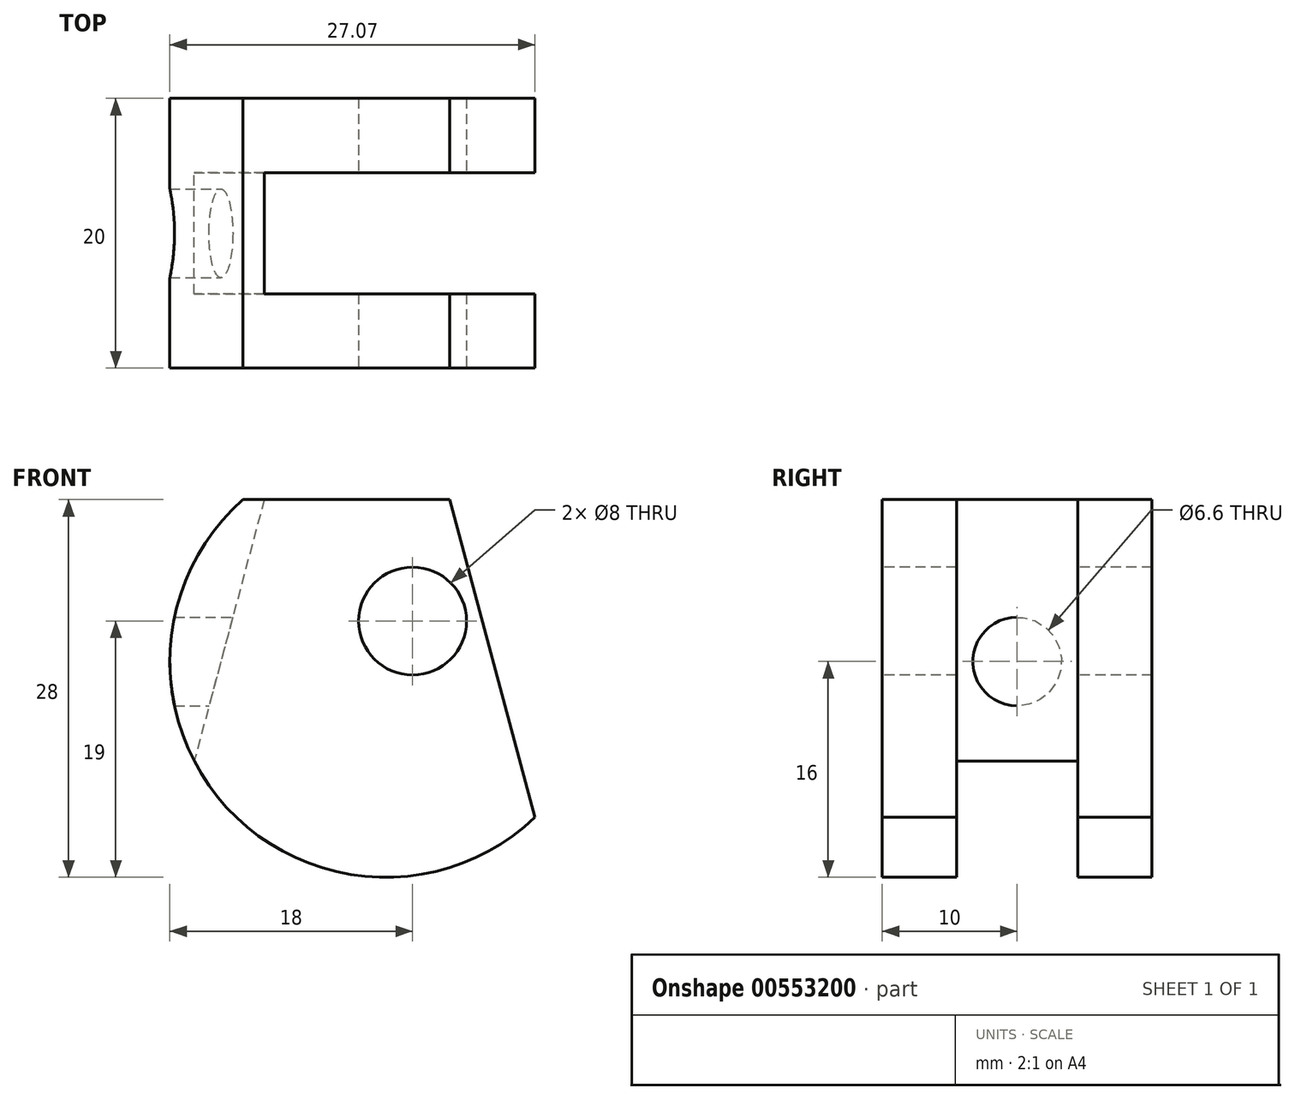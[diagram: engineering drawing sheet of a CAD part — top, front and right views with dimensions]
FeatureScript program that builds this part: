
annotation { "Feature Type Name" : "Feature", "Feature Type Description" : "" }
export const myFeature = defineFeature(function(context is Context, id is Id, definition is map)
    precondition{}
    {
        {
            var Q0;
            Q0=qCreatedBy(makeId("Front.planeOp"),FACE);
            var sketch = newSketch(context, id + "F0", { "sketchPlane" : qUnion([Q0])});
            skArc(sketch, "E0", {"start": v(-10.58, 12) * mm, "mid": v(-11.78, -10.83) * mm, "end": v(11.07, -11.55) * mm});
            skCircle(sketch, "E1", {"center": v(2, 3) * mm, "radius": 4 * mm, "construction": true});
            skLineSegment(sketch, "E2", {"start": v(-10.58, 12) * mm, "end": v(4.76, 12) * mm});
            skLineSegment(sketch, "E3", {"start": v(4.76, 12) * mm, "end": v(11.07, -11.55) * mm});
            skSolve(sketch);
        }
        {
            var Q0;
            Q0=qCreatedBy(makeId("Front.planeOp"),FACE);
            var sketch = newSketch(context, id + "F1", { "sketchPlane" : qUnion([Q0])});
            skLineSegment(sketch, "E4", {"start": v(-9, 12) * mm, "end": v(-16.5, -16) * mm});
            skLineSegment(sketch, "E5", {"start": v(-16.5, -16) * mm, "end": v(11.07, -16) * mm});
            skLineSegment(sketch, "E6", {"start": v(11.07, -16) * mm, "end": v(11.07, 12) * mm});
            skLineSegment(sketch, "E7", {"start": v(11.07, 12) * mm, "end": v(-9, 12) * mm});
            skSolve(sketch);
        }
        {
            var Q0;
            Q0 = qSketchRegion(id + "F0", true);
            extrude(context, id + "F2", {"entities" : qUnion([Q0]), "endBound" : BoundingType.SYMMETRIC, "depth" : 20 * mm, "offsetDistance" : 25 * mm});
        }
        {
            var Q0;
            Q0 = qSketchRegion(id + "F1", true);
            extrude(context, id + "F3", {"entities" : qUnion([Q0]), "operationType" : NewBodyOperationType.REMOVE, "endBound" : BoundingType.SYMMETRIC, "depth" : 9 * mm, "offsetDistance" : 25 * mm});
        }
        {
            var Q0;
            Q0=makeQuery(id+"F2.opExtrude","CAP_FACE",FACE,{"disambiguationData":[OSD([sQuery(id+"F0.wireOp",EDGE,"E0"),sQuery(id+"F0.wireOp",EDGE,"E2"),sQuery(id+"F0.wireOp",EDGE,"E3")])],"isStart":false});
            var sketch = newSketch(context, id + "F4", { "sketchPlane" : qUnion([Q0])});
            skPoint(sketch, "E8", {"position": v(2, 3) * mm});
            skSolve(sketch);
        }
        {
            var Q0;
            Q0=sQuery(id+"F4.wireOp",VERTEX,"E8");
            var Q1;
            Q1=makeQuery(id+"F2.opExtrude","SWEPT_BODY",BODY,{"disambiguationData":[OSD([sQuery(id+"F0.wireOp",EDGE,"E0"),sQuery(id+"F0.wireOp",EDGE,"E2"),sQuery(id+"F0.wireOp",EDGE,"E3")])]});
            hole(context, id + "F5", {"style" : HoleStyle.SIMPLE, "endStyle" : HoleEndStyle.THROUGH, "holeDiameter" : 8 * mm, "isTappedThrough" : true, "tappedDepth" : 11 * mm, "tapClearance" : 3, "locations" : qUnion([Q0]), "scope" : qUnion([Q1])});
        }
        {
            var Q0;
            Q0=qCreatedBy(makeId("Right.planeOp"),FACE);
            var sketch = newSketch(context, id + "F6", { "sketchPlane" : qUnion([Q0])});
            skPoint(sketch, "E9", {"position": v(0, 0) * mm});
            skSolve(sketch);
        }
        {
            var Q0;
            Q0=sQuery(id+"F6.wireOp",VERTEX,"E9");
            var Q1;
            Q1=makeQuery(id+"F2.opExtrude","SWEPT_BODY",BODY,{"disambiguationData":[OSD([sQuery(id+"F0.wireOp",EDGE,"E0"),sQuery(id+"F0.wireOp",EDGE,"E2"),sQuery(id+"F0.wireOp",EDGE,"E3")])]});
            hole(context, id + "F7", {"style" : HoleStyle.SIMPLE, "endStyle" : HoleEndStyle.THROUGH, "standardTappedOrClearance" : lookupTablePath({ "standard" : "ISO", "fit" : "Normal", "size" : "M6", "type" : "Clearance" }), "standardBlindInLast" : lookupTablePath({ "fit" : "Standard", "standard" : "ISO", "size" : "M6", "type" : "Clearance" }), "holeDiameter" : 6.6 * mm, "isTappedThrough" : true, "tappedDepth" : 11 * mm, "tapClearance" : 3, "locations" : qUnion([Q0]), "scope" : qUnion([Q1])});
        }
    });
